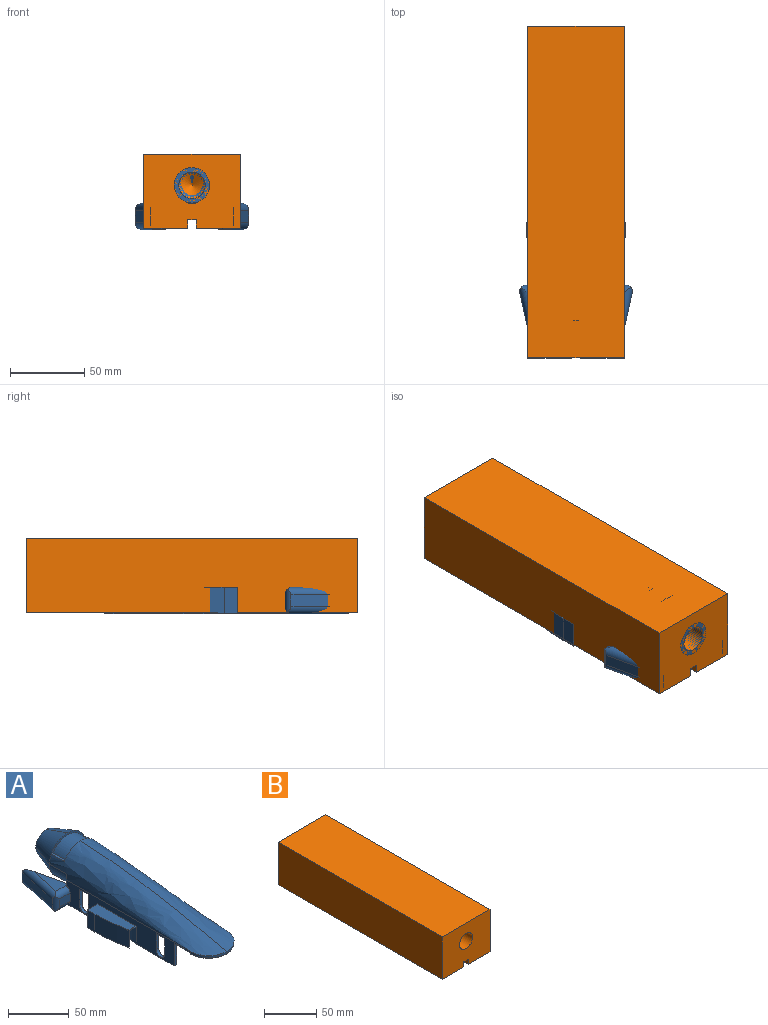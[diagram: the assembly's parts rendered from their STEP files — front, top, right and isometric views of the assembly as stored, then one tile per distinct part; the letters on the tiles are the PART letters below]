
ASSEMBLY  parts=2 mates=1
PART A: 90 faces, bbox 81.4x216.2x55.5 mm
  f0: plane 36x25mm, normal (0,0,-1), area 862.6mm2, adj f5,f10,f12,f13,f46,f54,f55,f87
  f1: cone r=11.9mm half-angle=20deg, axis (0,-1,0), area 738.4mm2, adj f13,f46,f47,f70,f71,f86,f87,f88
  f2: plane 42x16mm, normal (0,1,0), area 204mm2, adj f6,f9,f10,f12,f21,f78,f82,f85
  f3: plane 42x16mm, normal (0,1,0), area 204mm2, adj f6,f10,f12,f17,f21,f79,f80,f83
  f4: plane 42x16mm, normal (0,-1,0), area 204mm2, adj f6,f10,f12,f17,f21,f78,f82,f85
  f5: plane 42x16mm, normal (0,-1,0), area 204mm2, adj f0,f6,f10,f12,f21,f79,f80,f83
  f6: plane 145.24x24.24mm, normal (-1,0,0), area 1758.7mm2, adj f2,f3,f4,f5,f7,f8,f15,f23
  f7: plane 114.48x15mm, normal (0,0,-1), area 642mm2, adj f6,f12,f24,f30,f31,f38,f56,f65
  f8: plane 60.45x3mm, normal (0,0,-1), area 161.4mm2, adj f6,f12,f23,f37
  f9: plane 36x11mm, normal (0,0,-1), area 396mm2, adj f2,f10,f12,f23
  f10: plane 125x19mm, normal (-1,0,0), area 1540.2mm2, adj f0,f2,f3,f4,f5,f9,f11,f17
  f11: plane 114.48x15mm, normal (0,0,-1), area 642mm2, adj f10,f21,f33,f34,f36,f40,f59,f60
  f12: plane 125x19mm, normal (1,0,0), area 1540.2mm2, adj f0,f2,f3,f4,f5,f7,f8,f9
  f13: cylinder r=21mm len=20mm, axis (0,-1,0), area 231.6mm2, adj f0,f1,f15,f55,f87
  f14: plane 32.48x14.43mm, normal (0,0,1), area 234.4mm2, adj f59,f63,f64
  f15: bspline ~185x27.09mm, area 5148.1mm2, adj f6,f13,f16,f20,f27,f50,f55,f71
  f16: bspline ~185x27mm, area 5148.1mm2, adj f15,f19,f21,f27,f46,f50,f54,f70
  f17: plane 79x36mm, normal (0,0,-1), area 2844mm2, adj f3,f4,f10,f12
  f18: plane 37.99x12.05mm, normal (0,-1,0), area 88.3mm2, adj f19,f20,f51,f70,f71
  f19: plane 15.06x2.65mm, normal (0,0,1), area 34.1mm2, adj f16,f18,f50,f51
  f20: plane 15.06x2.65mm, normal (0,0,1), area 34.1mm2, adj f15,f18,f50,f51
  f21: plane 145.24x24.24mm, normal (1,0,0), area 1758.7mm2, adj f2,f3,f4,f5,f11,f16,f22,f23
  f22: plane 60.45x3mm, normal (0,0,-1), area 161.4mm2, adj f10,f21,f23,f41
  f23: plane 42x22.5mm, normal (0,-1,0), area 261mm2, adj f6,f8,f9,f10,f12,f21,f22,f44
  f24: plane 18x8.92mm, normal (-1,0,0), area 160.6mm2, adj f7,f25,f30,f31
  f25: plane 44.5x12mm, normal (0,0,1), area 483.3mm2, adj f6,f24,f30,f31,f52
  f26: plane 40x20mm, normal (0,0,-1), area 628.3mm2, adj f43,f45
  f27: cylinder r=21mm len=42mm, axis (0,0,1), area 131.9mm2, adj f6,f15,f16,f21,f43,f45
  f28: plane 32.48x14.43mm, normal (0,0,1), area 234.4mm2, adj f56,f67,f69
  f29: plane 12.1x8mm, normal (0,-1,0), area 96.8mm2, adj f6,f65,f67,f68
  f30: plane 18x12mm, normal (0,1,0), area 216mm2, adj f6,f7,f24,f25
  f31: cylinder r=205mm len=36.08mm, axis (0,0,1), area 654.2mm2, adj f7,f24,f25,f38,f52
  f32: plane 12.1x8mm, normal (0,-1,0), area 96.8mm2, adj f21,f61,f62,f63
  f33: cylinder r=205mm len=36.08mm, axis (0,0,1), area 654.2mm2, adj f11,f34,f35,f40,f53
  f34: plane 18x8.92mm, normal (1,0,0), area 160.6mm2, adj f11,f33,f35,f36
  f35: plane 44.5x12mm, normal (0,0,1), area 483.3mm2, adj f21,f33,f34,f36,f53
  f36: plane 18x12mm, normal (0,1,0), area 216mm2, adj f11,f21,f34,f35
  f37: extruded ~17.5x16.45mm, area 285mm2, adj f6,f8,f12,f39,f52
  f38: extruded ~45x17.5mm, area 792.2mm2, adj f7,f12,f31,f39,f52
  f39: plane 45x11mm, normal (0,0,-1), area 281.1mm2, adj f12,f37,f38,f52
  f40: extruded ~45x17.5mm, area 792.2mm2, adj f10,f11,f33,f42,f53
  f41: extruded ~17.5x16.45mm, area 285mm2, adj f10,f21,f22,f42,f53
  f42: plane 45x11mm, normal (0,0,-1), area 281.1mm2, adj f10,f40,f41,f53
  f43: plane 42x1.5mm, normal (0,1,0), area 62.6mm2, adj f26,f27,f44,f45
  f44: plane 42x19mm, normal (0,0,-1), area 798mm2, adj f6,f21,f23,f43
  f45: torus R=20mm, axis (0,0,-1), area 101.8mm2, adj f26,f27,f43
  f46: cylinder r=21mm len=20mm, axis (0,-1,0), area 231.6mm2, adj f0,f1,f16,f54,f88
  f47: plane 23.84x23.84mm, normal (0,1,0), area 196mm2, adj f1,f49,f70,f71
  f48: cone r=0mm half-angle=59deg, axis (0,1,0), area 290.3mm2, adj f49
  f49: cylinder r=8.9mm len=52mm, axis (0,1,0), area 2907.9mm2, adj f47,f48
  f50: plane 38.02x12.31mm, normal (0,1,0), area 86mm2, adj f15,f16,f19,f20,f51
  f51: bspline ~33.47x15mm, area 605.4mm2, adj f18,f19,f20,f50
  f52: cylinder r=0.5mm len=8.12mm, axis (1,0,0), area 12.6mm2, adj f6,f25,f31,f37,f38,f39
  f53: cylinder r=0.5mm len=8.12mm, axis (-1,0,0), area 12.6mm2, adj f21,f33,f35,f40,f41,f42
  f54: plane 12.47x3.48mm, normal (0,1,0), area 14.4mm2, adj f0,f10,f16,f21,f46,f63
  f55: plane 12.47x3.48mm, normal (0,1,0), area 14.4mm2, adj f0,f6,f12,f13,f15,f67
  f56: plane 49.5x22.5mm, normal (0.98,0.22,0), area 804.4mm2, adj f7,f12,f28,f57,f66,f67,f69
  f57: plane 45x10mm, normal (-0.98,0.22,0), area 368.8mm2, adj f56,f66,f68,f69
  f58: plane 45x10mm, normal (0.98,0.22,0), area 368.8mm2, adj f59,f60,f62,f64
  f59: plane 49.5x22.5mm, normal (-0.98,0.22,0), area 804.4mm2, adj f10,f11,f14,f58,f60,f63,f64
  f60: cylinder r=5mm len=48.07mm, axis (0.22,-0.98,0), area 324.1mm2, adj f11,f58,f59,f61,f62
  f61: cylinder r=5mm len=15.82mm, axis (1,0,0), area 108.8mm2, adj f11,f21,f32,f60,f62
  f62: cylinder r=5mm len=15.44mm, axis (0,0,-1), area 80.2mm2, adj f32,f58,f60,f61,f63,f64
  f63: cylinder r=5mm len=18.82mm, axis (-1,0,0), area 111.7mm2, adj f14,f21,f32,f54,f59,f62,f64
  f64: cylinder r=5mm len=48.07mm, axis (-0.22,0.98,0), area 324.1mm2, adj f14,f58,f59,f62,f63
  f65: cylinder r=5mm len=15.82mm, axis (-1,0,0), area 108.8mm2, adj f6,f7,f29,f66,f68
  f66: cylinder r=5mm len=48.07mm, axis (0.22,0.98,0), area 324.1mm2, adj f7,f56,f57,f65,f68
  f67: cylinder r=5mm len=18.82mm, axis (1,0,0), area 111.7mm2, adj f6,f28,f29,f55,f56,f68,f69
  f68: cylinder r=5mm len=15.44mm, axis (0,0,-1), area 80.2mm2, adj f29,f57,f65,f66,f67,f69
  f69: cylinder r=5mm len=48.07mm, axis (-0.22,-0.98,0), area 324.1mm2, adj f28,f56,f57,f67,f68
  f70: bspline ~25x21mm, area 687.4mm2, adj f1,f16,f18,f47,f71
  f71: bspline ~25x21mm, area 687.4mm2, adj f1,f15,f18,f47,f70
  f72: plane 5.5x2mm, normal (1,0,0), area 11mm2, adj f7,f73,f74,f81
  f73: plane 5.5x2mm, normal (0,0,-1), area 11mm2, adj f12,f72,f74,f81
  f74: plane 2x2mm, normal (0,-1,0), area 4mm2, adj f7,f12,f72,f73
  f75: plane 5.5x2mm, normal (0,0,-1), area 11mm2, adj f10,f76,f77,f84
  f76: plane 5.5x2mm, normal (-1,0,0), area 11mm2, adj f11,f75,f77,f84
  f77: plane 2x2mm, normal (0,-1,0), area 4mm2, adj f10,f11,f75,f76
  f78: plane 42x10mm, normal (0,0,-1), area 420mm2, adj f2,f4,f6,f21
  f79: plane 42x10mm, normal (0,0,-1), area 420mm2, adj f3,f5,f6,f21
  f80: cylinder r=5mm len=10mm, axis (-1,0,0), area 47.1mm2, adj f3,f5,f6,f12
  f81: plane 2x2mm, normal (0,1,0), area 4mm2, adj f7,f12,f72,f73
  f82: cylinder r=5mm len=10mm, axis (-1,0,0), area 47.1mm2, adj f2,f4,f6,f12
  f83: cylinder r=5mm len=10mm, axis (1,0,0), area 47.1mm2, adj f3,f5,f10,f21
  f84: plane 2x2mm, normal (0,1,0), area 4mm2, adj f10,f11,f75,f76
  f85: cylinder r=5mm len=10mm, axis (1,0,0), area 47.1mm2, adj f2,f4,f10,f21
  f86: plane 34.48x24.73mm, normal (0,0,-1), area 535.8mm2, adj f1,f89
  f87: bspline ~11x1mm, area 9.1mm2, adj f0,f1,f13,f89
  f88: bspline ~11x1mm, area 9.1mm2, adj f0,f1,f46,f89
  f89: bspline ~34.47x11mm, area 381.6mm2, adj f0,f86,f87,f88
PART B: 12 faces, bbox 65x223x50 mm
  f0: plane 223x50mm, normal (-1,0,0), area 11150mm2, adj f1,f7,f8,f9
  f1: plane 223x29.5mm, normal (0,0,-1), area 6578.5mm2, adj f0,f2,f8,f9
  f2: plane 223x6mm, normal (1,0,0), area 1338mm2, adj f1,f3,f8,f9
  f3: plane 223x6mm, normal (0,0,-1), area 1338mm2, adj f2,f4,f8,f9
  f4: plane 223x6mm, normal (-1,0,0), area 1338mm2, adj f3,f5,f8,f9
  f5: plane 223x29.5mm, normal (0,0,-1), area 6578.5mm2, adj f4,f6,f8,f9
  f6: plane 223x50mm, normal (1,0,0), area 11150mm2, adj f5,f7,f8,f9
  f7: plane 223x65mm, normal (0,0,1), area 14495mm2, adj f0,f6,f8,f9
  f8: plane 65x50mm, normal (0,1,0), area 3214mm2, adj f0,f1,f2,f3,f4,f5,f6,f7
  f9: plane 65x50mm, normal (0,-1,0), area 2965.2mm2, adj f0,f1,f2,f3,f4,f5,f6,f7
  f10: cone r=0mm half-angle=59deg, axis (0,-1,0), area 290.3mm2, adj f11
  f11: cylinder r=8.9mm len=52mm, axis (0,-1,0), area 2907.9mm2, adj f9,f10
PLACE A rot(axis=(0,0,1),180deg) t=(14.8,-38.8,-36.65)mm
PLACE B t=(-50.2,-38.8,-35.65)mm fixed
MATE fastened B.f10 <-> A.f1  axis (0,-1,0) through (-17.7,-38.8,-6.65)mm
